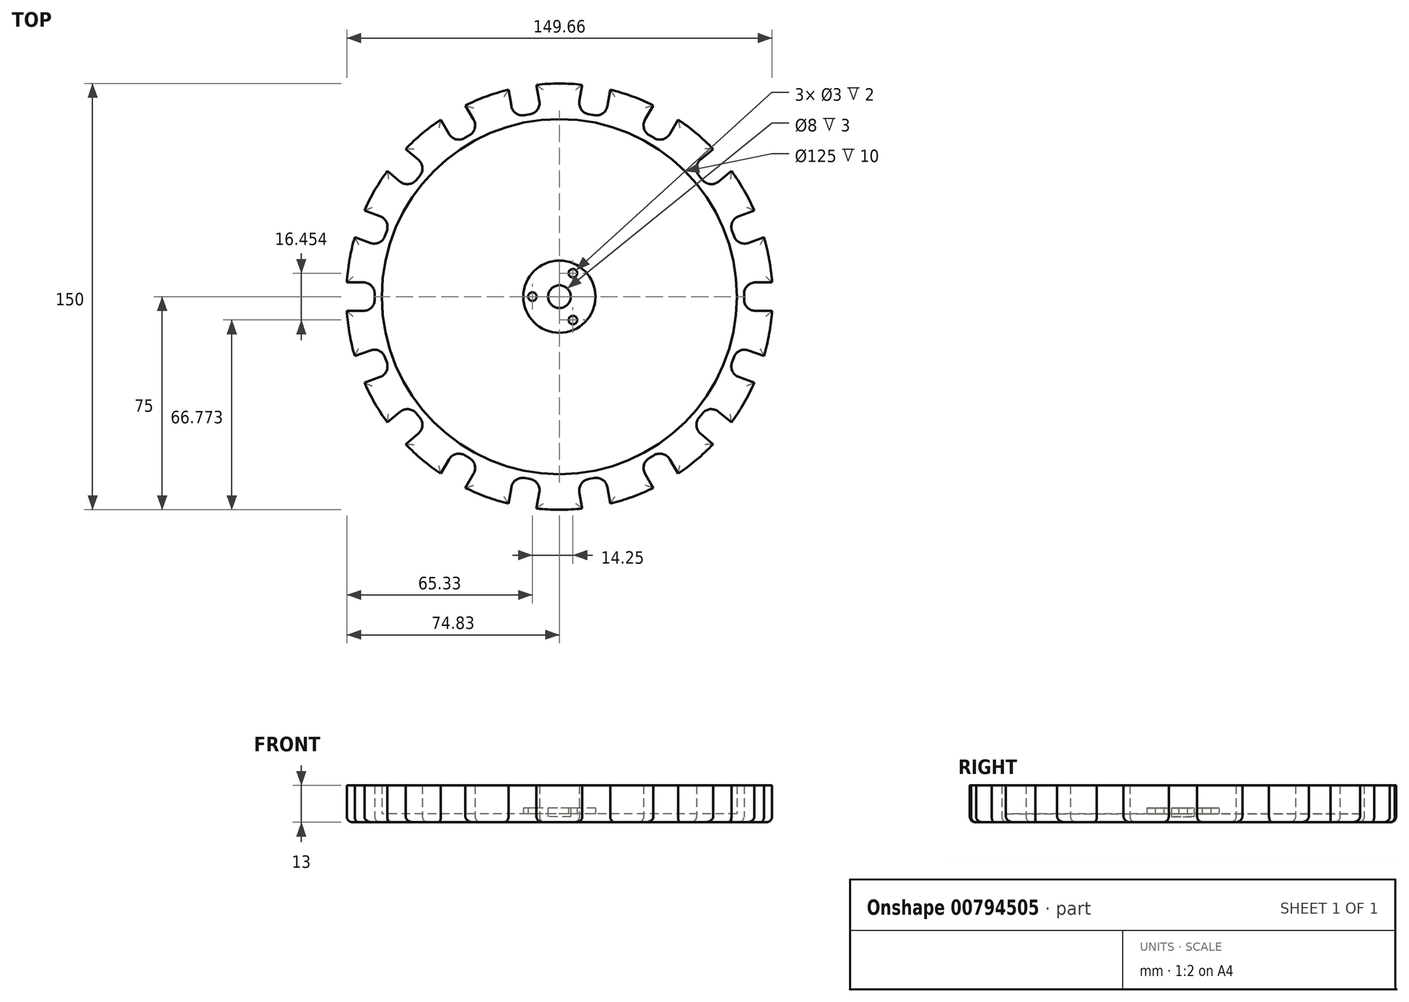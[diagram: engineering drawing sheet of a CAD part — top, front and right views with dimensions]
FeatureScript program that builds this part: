
annotation { "Feature Type Name" : "Feature", "Feature Type Description" : "" }
export const myFeature = defineFeature(function(context is Context, id is Id, definition is map)
    precondition{}
    {
        {
            var Q0;
            Q0=qCreatedBy(makeId("Top.planeOp"),FACE);
            var sketch = newSketch(context, id + "F0", { "sketchPlane" : qUnion([Q0])});
            skCircle(sketch, "E0", {"center": v(0, 0) * mm, "radius": 75 * mm});
            skCircle(sketch, "E1", {"center": v(0, 0) * mm, "radius": 62.5 * mm});
            skLineSegment(sketch, "E2", {"start": v(0, 0) * mm, "end": v(-124.02, 0) * mm, "construction": true});
            skPoint(sketch, "E3", {"position": v(-75, 0) * mm});
            skLineSegment(sketch, "E4.bottom", {"start": v(-75, -5) * mm, "end": v(-69, -5) * mm});
            skLineSegment(sketch, "E4.top", {"start": v(-75, 5) * mm, "end": v(-69, 5) * mm});
            skLineSegment(sketch, "E4.left", {"start": v(-75, -5) * mm, "end": v(-75, 5) * mm});
            skLineSegment(sketch, "E4.right", {"start": v(-65, -1) * mm, "end": v(-65, 1) * mm});
            skPoint(sketch, "E4.middle", {"position": v(-70, 0) * mm});
            skPoint(sketch, "E5.visualSharp", {"position": v(-65, 5) * mm});
            skArc(sketch, "E5.filletArc", {"start": v(-65, 1) * mm, "mid": v(-66.17, 3.83) * mm, "end": v(-69, 5) * mm});
            skPoint(sketch, "E6.visualSharp", {"position": v(-65, -5) * mm});
            skArc(sketch, "E6.filletArc", {"start": v(-69, -5) * mm, "mid": v(-66.17, -3.83) * mm, "end": v(-65, -1) * mm});
            skPoint(sketch, "E7.center", {"position": v(1.56, 0) * mm});
            skCircle(sketch, "E8", {"center": v(0, 0) * mm, "radius": 4 * mm});
            skCircle(sketch, "E9", {"center": v(0, 0) * mm, "radius": 12.7 * mm});
            skCircle(sketch, "E10", {"center": v(0, 0) * mm, "radius": 9.5 * mm, "construction": true});
            skCircle(sketch, "E11", {"center": v(-9.5, 0) * mm, "radius": 1.5 * mm});
            skCircle(sketch, "E12.1.0", {"center": v(-4.75, -8.23) * mm, "radius": 1.5 * mm});
            skCircle(sketch, "E12.2.0", {"center": v(4.75, -8.23) * mm, "radius": 1.5 * mm});
            skCircle(sketch, "E12.3.0", {"center": v(9.5, 0) * mm, "radius": 1.5 * mm});
            skCircle(sketch, "E12.4.0", {"center": v(4.75, 8.23) * mm, "radius": 1.5 * mm});
            skCircle(sketch, "E12.5.0", {"center": v(-4.75, 8.23) * mm, "radius": 1.5 * mm});
            skPoint(sketch, "E13.1.0", {"position": v(-62.8, -17.53) * mm});
            skPoint(sketch, "E13.1.1", {"position": v(-70.48, -25.65) * mm});
            skPoint(sketch, "E13.1.2", {"position": v(-59.37, -26.93) * mm});
            skPoint(sketch, "E13.1.3", {"position": v(-65.78, -23.94) * mm});
            skArc(sketch, "E13.1.4", {"start": v(-63.13, -28.3) * mm, "mid": v(-60.87, -26.23) * mm, "end": v(-60.74, -23.17) * mm});
            skArc(sketch, "E13.1.5", {"start": v(-61.42, -21.3) * mm, "mid": v(-63.5, -19.03) * mm, "end": v(-66.55, -18.9) * mm});
            skLineSegment(sketch, "E13.1.6", {"start": v(-68.77, -30.35) * mm, "end": v(-72.19, -20.95) * mm});
            skLineSegment(sketch, "E13.1.7", {"start": v(-60.74, -23.17) * mm, "end": v(-61.42, -21.3) * mm});
            skLineSegment(sketch, "E13.1.8", {"start": v(-72.19, -20.95) * mm, "end": v(-66.55, -18.9) * mm});
            skLineSegment(sketch, "E13.1.9", {"start": v(-68.77, -30.35) * mm, "end": v(-63.13, -28.3) * mm});
            skPoint(sketch, "E13.2.0", {"position": v(-53, -37.95) * mm});
            skPoint(sketch, "E13.2.1", {"position": v(-57.45, -48.2) * mm});
            skPoint(sketch, "E13.2.2", {"position": v(-46.58, -45.61) * mm});
            skPoint(sketch, "E13.2.3", {"position": v(-53.62, -45) * mm});
            skArc(sketch, "E13.2.4", {"start": v(-49.64, -48.18) * mm, "mid": v(-48.23, -45.47) * mm, "end": v(-49.15, -42.55) * mm});
            skArc(sketch, "E13.2.5", {"start": v(-50.44, -41.02) * mm, "mid": v(-53.15, -39.6) * mm, "end": v(-56.07, -40.52) * mm});
            skLineSegment(sketch, "E13.2.6", {"start": v(-54.24, -52.04) * mm, "end": v(-60.67, -44.38) * mm});
            skLineSegment(sketch, "E13.2.7", {"start": v(-49.15, -42.55) * mm, "end": v(-50.44, -41.02) * mm});
            skLineSegment(sketch, "E13.2.8", {"start": v(-60.67, -44.38) * mm, "end": v(-56.07, -40.52) * mm});
            skLineSegment(sketch, "E13.2.9", {"start": v(-54.24, -52.04) * mm, "end": v(-49.64, -48.18) * mm});
            skPoint(sketch, "E13.3.0", {"position": v(-36.83, -53.8) * mm});
            skPoint(sketch, "E13.3.1", {"position": v(-37.5, -64.95) * mm});
            skPoint(sketch, "E13.3.2", {"position": v(-28.17, -58.8) * mm});
            skPoint(sketch, "E13.3.3", {"position": v(-35, -60.62) * mm});
            skArc(sketch, "E13.3.4", {"start": v(-30.17, -62.26) * mm, "mid": v(-29.77, -59.22) * mm, "end": v(-31.63, -56.8) * mm});
            skArc(sketch, "E13.3.5", {"start": v(-33.37, -55.8) * mm, "mid": v(-36.4, -55.4) * mm, "end": v(-38.83, -57.26) * mm});
            skLineSegment(sketch, "E13.3.6", {"start": v(-33.17, -67.45) * mm, "end": v(-41.83, -62.45) * mm});
            skLineSegment(sketch, "E13.3.7", {"start": v(-31.63, -56.8) * mm, "end": v(-33.37, -55.8) * mm});
            skLineSegment(sketch, "E13.3.8", {"start": v(-41.83, -62.45) * mm, "end": v(-38.83, -57.26) * mm});
            skLineSegment(sketch, "E13.3.9", {"start": v(-33.17, -67.45) * mm, "end": v(-30.17, -62.26) * mm});
            skPoint(sketch, "E13.4.0", {"position": v(-16.21, -63.14) * mm});
            skPoint(sketch, "E13.4.1", {"position": v(-13.02, -73.86) * mm});
            skPoint(sketch, "E13.4.2", {"position": v(-6.36, -64.88) * mm});
            skPoint(sketch, "E13.4.3", {"position": v(-12.16, -68.94) * mm});
            skArc(sketch, "E13.4.4", {"start": v(-7.06, -68.82) * mm, "mid": v(-7.72, -65.83) * mm, "end": v(-10.3, -64.19) * mm});
            skArc(sketch, "E13.4.5", {"start": v(-12.27, -63.84) * mm, "mid": v(-15.26, -64.5) * mm, "end": v(-16.9, -67.08) * mm});
            skLineSegment(sketch, "E13.4.6", {"start": v(-8.1, -74.73) * mm, "end": v(-17.95, -73) * mm});
            skLineSegment(sketch, "E13.4.7", {"start": v(-10.3, -64.19) * mm, "end": v(-12.27, -63.84) * mm});
            skLineSegment(sketch, "E13.4.8", {"start": v(-17.95, -73) * mm, "end": v(-16.9, -67.08) * mm});
            skLineSegment(sketch, "E13.4.9", {"start": v(-8.1, -74.73) * mm, "end": v(-7.06, -68.82) * mm});
            skPoint(sketch, "E13.5.0", {"position": v(6.36, -64.88) * mm});
            skPoint(sketch, "E13.5.1", {"position": v(13.02, -73.86) * mm});
            skPoint(sketch, "E13.5.2", {"position": v(16.21, -63.14) * mm});
            skPoint(sketch, "E13.5.3", {"position": v(12.16, -68.94) * mm});
            skArc(sketch, "E13.5.4", {"start": v(16.9, -67.08) * mm, "mid": v(15.26, -64.5) * mm, "end": v(12.27, -63.84) * mm});
            skArc(sketch, "E13.5.5", {"start": v(10.3, -64.19) * mm, "mid": v(7.72, -65.83) * mm, "end": v(7.06, -68.82) * mm});
            skLineSegment(sketch, "E13.5.6", {"start": v(17.95, -73) * mm, "end": v(8.1, -74.73) * mm});
            skLineSegment(sketch, "E13.5.7", {"start": v(12.27, -63.84) * mm, "end": v(10.3, -64.19) * mm});
            skLineSegment(sketch, "E13.5.8", {"start": v(8.1, -74.73) * mm, "end": v(7.06, -68.82) * mm});
            skLineSegment(sketch, "E13.5.9", {"start": v(17.95, -73) * mm, "end": v(16.9, -67.08) * mm});
            skPoint(sketch, "E13.6.0", {"position": v(28.17, -58.8) * mm});
            skPoint(sketch, "E13.6.1", {"position": v(37.5, -64.95) * mm});
            skPoint(sketch, "E13.6.2", {"position": v(36.83, -53.8) * mm});
            skPoint(sketch, "E13.6.3", {"position": v(35, -60.62) * mm});
            skArc(sketch, "E13.6.4", {"start": v(38.83, -57.26) * mm, "mid": v(36.4, -55.4) * mm, "end": v(33.37, -55.8) * mm});
            skArc(sketch, "E13.6.5", {"start": v(31.63, -56.8) * mm, "mid": v(29.77, -59.22) * mm, "end": v(30.17, -62.26) * mm});
            skLineSegment(sketch, "E13.6.6", {"start": v(41.83, -62.45) * mm, "end": v(33.17, -67.45) * mm});
            skLineSegment(sketch, "E13.6.7", {"start": v(33.37, -55.8) * mm, "end": v(31.63, -56.8) * mm});
            skLineSegment(sketch, "E13.6.8", {"start": v(33.17, -67.45) * mm, "end": v(30.17, -62.26) * mm});
            skLineSegment(sketch, "E13.6.9", {"start": v(41.83, -62.45) * mm, "end": v(38.83, -57.26) * mm});
            skPoint(sketch, "E13.7.0", {"position": v(46.58, -45.61) * mm});
            skPoint(sketch, "E13.7.1", {"position": v(57.45, -48.2) * mm});
            skPoint(sketch, "E13.7.2", {"position": v(53, -37.95) * mm});
            skPoint(sketch, "E13.7.3", {"position": v(53.62, -45) * mm});
            skArc(sketch, "E13.7.4", {"start": v(56.07, -40.52) * mm, "mid": v(53.15, -39.6) * mm, "end": v(50.44, -41.02) * mm});
            skArc(sketch, "E13.7.5", {"start": v(49.15, -42.55) * mm, "mid": v(48.23, -45.47) * mm, "end": v(49.64, -48.18) * mm});
            skLineSegment(sketch, "E13.7.6", {"start": v(60.67, -44.38) * mm, "end": v(54.24, -52.04) * mm});
            skLineSegment(sketch, "E13.7.7", {"start": v(50.44, -41.02) * mm, "end": v(49.15, -42.55) * mm});
            skLineSegment(sketch, "E13.7.8", {"start": v(54.24, -52.04) * mm, "end": v(49.64, -48.18) * mm});
            skLineSegment(sketch, "E13.7.9", {"start": v(60.67, -44.38) * mm, "end": v(56.07, -40.52) * mm});
            skPoint(sketch, "E13.8.0", {"position": v(59.37, -26.93) * mm});
            skPoint(sketch, "E13.8.1", {"position": v(70.48, -25.65) * mm});
            skPoint(sketch, "E13.8.2", {"position": v(62.8, -17.53) * mm});
            skPoint(sketch, "E13.8.3", {"position": v(65.78, -23.94) * mm});
            skArc(sketch, "E13.8.4", {"start": v(66.55, -18.9) * mm, "mid": v(63.5, -19.03) * mm, "end": v(61.42, -21.3) * mm});
            skArc(sketch, "E13.8.5", {"start": v(60.74, -23.17) * mm, "mid": v(60.87, -26.23) * mm, "end": v(63.13, -28.3) * mm});
            skLineSegment(sketch, "E13.8.6", {"start": v(72.19, -20.95) * mm, "end": v(68.77, -30.35) * mm});
            skLineSegment(sketch, "E13.8.7", {"start": v(61.42, -21.3) * mm, "end": v(60.74, -23.17) * mm});
            skLineSegment(sketch, "E13.8.8", {"start": v(68.77, -30.35) * mm, "end": v(63.13, -28.3) * mm});
            skLineSegment(sketch, "E13.8.9", {"start": v(72.19, -20.95) * mm, "end": v(66.55, -18.9) * mm});
            skPoint(sketch, "E13.9.0", {"position": v(65, -5) * mm});
            skPoint(sketch, "E13.9.1", {"position": v(75, 0) * mm});
            skPoint(sketch, "E13.9.2", {"position": v(65, 5) * mm});
            skPoint(sketch, "E13.9.3", {"position": v(70, 0) * mm});
            skArc(sketch, "E13.9.4", {"start": v(69, 5) * mm, "mid": v(66.17, 3.83) * mm, "end": v(65, 1) * mm});
            skArc(sketch, "E13.9.5", {"start": v(65, -1) * mm, "mid": v(66.17, -3.83) * mm, "end": v(69, -5) * mm});
            skLineSegment(sketch, "E13.9.6", {"start": v(75, 5) * mm, "end": v(75, -5) * mm});
            skLineSegment(sketch, "E13.9.7", {"start": v(65, 1) * mm, "end": v(65, -1) * mm});
            skLineSegment(sketch, "E13.9.8", {"start": v(75, -5) * mm, "end": v(69, -5) * mm});
            skLineSegment(sketch, "E13.9.9", {"start": v(75, 5) * mm, "end": v(69, 5) * mm});
            skPoint(sketch, "E13.10.0", {"position": v(62.8, 17.53) * mm});
            skPoint(sketch, "E13.10.1", {"position": v(70.48, 25.65) * mm});
            skPoint(sketch, "E13.10.2", {"position": v(59.37, 26.93) * mm});
            skPoint(sketch, "E13.10.3", {"position": v(65.78, 23.94) * mm});
            skArc(sketch, "E13.10.4", {"start": v(63.13, 28.3) * mm, "mid": v(60.87, 26.23) * mm, "end": v(60.74, 23.17) * mm});
            skArc(sketch, "E13.10.5", {"start": v(61.42, 21.3) * mm, "mid": v(63.5, 19.03) * mm, "end": v(66.55, 18.9) * mm});
            skLineSegment(sketch, "E13.10.6", {"start": v(68.77, 30.35) * mm, "end": v(72.19, 20.95) * mm});
            skLineSegment(sketch, "E13.10.7", {"start": v(60.74, 23.17) * mm, "end": v(61.42, 21.3) * mm});
            skLineSegment(sketch, "E13.10.8", {"start": v(72.19, 20.95) * mm, "end": v(66.55, 18.9) * mm});
            skLineSegment(sketch, "E13.10.9", {"start": v(68.77, 30.35) * mm, "end": v(63.13, 28.3) * mm});
            skPoint(sketch, "E13.11.0", {"position": v(53, 37.95) * mm});
            skPoint(sketch, "E13.11.1", {"position": v(57.45, 48.2) * mm});
            skPoint(sketch, "E13.11.2", {"position": v(46.58, 45.61) * mm});
            skPoint(sketch, "E13.11.3", {"position": v(53.62, 45) * mm});
            skArc(sketch, "E13.11.4", {"start": v(49.64, 48.18) * mm, "mid": v(48.23, 45.47) * mm, "end": v(49.15, 42.55) * mm});
            skArc(sketch, "E13.11.5", {"start": v(50.44, 41.02) * mm, "mid": v(53.15, 39.6) * mm, "end": v(56.07, 40.52) * mm});
            skLineSegment(sketch, "E13.11.6", {"start": v(54.24, 52.04) * mm, "end": v(60.67, 44.38) * mm});
            skLineSegment(sketch, "E13.11.7", {"start": v(49.15, 42.55) * mm, "end": v(50.44, 41.02) * mm});
            skLineSegment(sketch, "E13.11.8", {"start": v(60.67, 44.38) * mm, "end": v(56.07, 40.52) * mm});
            skLineSegment(sketch, "E13.11.9", {"start": v(54.24, 52.04) * mm, "end": v(49.64, 48.18) * mm});
            skPoint(sketch, "E13.12.0", {"position": v(36.83, 53.8) * mm});
            skPoint(sketch, "E13.12.1", {"position": v(37.5, 64.95) * mm});
            skPoint(sketch, "E13.12.2", {"position": v(28.17, 58.8) * mm});
            skPoint(sketch, "E13.12.3", {"position": v(35, 60.62) * mm});
            skArc(sketch, "E13.12.4", {"start": v(30.17, 62.26) * mm, "mid": v(29.77, 59.22) * mm, "end": v(31.63, 56.8) * mm});
            skArc(sketch, "E13.12.5", {"start": v(33.37, 55.8) * mm, "mid": v(36.4, 55.4) * mm, "end": v(38.83, 57.26) * mm});
            skLineSegment(sketch, "E13.12.6", {"start": v(33.17, 67.45) * mm, "end": v(41.83, 62.45) * mm});
            skLineSegment(sketch, "E13.12.7", {"start": v(31.63, 56.8) * mm, "end": v(33.37, 55.8) * mm});
            skLineSegment(sketch, "E13.12.8", {"start": v(41.83, 62.45) * mm, "end": v(38.83, 57.26) * mm});
            skLineSegment(sketch, "E13.12.9", {"start": v(33.17, 67.45) * mm, "end": v(30.17, 62.26) * mm});
            skPoint(sketch, "E13.13.0", {"position": v(16.21, 63.14) * mm});
            skPoint(sketch, "E13.13.1", {"position": v(13.02, 73.86) * mm});
            skPoint(sketch, "E13.13.2", {"position": v(6.36, 64.88) * mm});
            skPoint(sketch, "E13.13.3", {"position": v(12.16, 68.94) * mm});
            skArc(sketch, "E13.13.4", {"start": v(7.06, 68.82) * mm, "mid": v(7.72, 65.83) * mm, "end": v(10.3, 64.19) * mm});
            skArc(sketch, "E13.13.5", {"start": v(12.27, 63.84) * mm, "mid": v(15.26, 64.5) * mm, "end": v(16.9, 67.08) * mm});
            skLineSegment(sketch, "E13.13.6", {"start": v(8.1, 74.73) * mm, "end": v(17.95, 73) * mm});
            skLineSegment(sketch, "E13.13.7", {"start": v(10.3, 64.19) * mm, "end": v(12.27, 63.84) * mm});
            skLineSegment(sketch, "E13.13.8", {"start": v(17.95, 73) * mm, "end": v(16.9, 67.08) * mm});
            skLineSegment(sketch, "E13.13.9", {"start": v(8.1, 74.73) * mm, "end": v(7.06, 68.82) * mm});
            skPoint(sketch, "E13.14.0", {"position": v(-6.36, 64.88) * mm});
            skPoint(sketch, "E13.14.1", {"position": v(-13.02, 73.86) * mm});
            skPoint(sketch, "E13.14.2", {"position": v(-16.21, 63.14) * mm});
            skPoint(sketch, "E13.14.3", {"position": v(-12.16, 68.94) * mm});
            skArc(sketch, "E13.14.4", {"start": v(-16.9, 67.08) * mm, "mid": v(-15.26, 64.5) * mm, "end": v(-12.27, 63.84) * mm});
            skArc(sketch, "E13.14.5", {"start": v(-10.3, 64.19) * mm, "mid": v(-7.72, 65.83) * mm, "end": v(-7.06, 68.82) * mm});
            skLineSegment(sketch, "E13.14.6", {"start": v(-17.95, 73) * mm, "end": v(-8.1, 74.73) * mm});
            skLineSegment(sketch, "E13.14.7", {"start": v(-12.27, 63.84) * mm, "end": v(-10.3, 64.19) * mm});
            skLineSegment(sketch, "E13.14.8", {"start": v(-8.1, 74.73) * mm, "end": v(-7.06, 68.82) * mm});
            skLineSegment(sketch, "E13.14.9", {"start": v(-17.95, 73) * mm, "end": v(-16.9, 67.08) * mm});
            skPoint(sketch, "E13.15.0", {"position": v(-28.17, 58.8) * mm});
            skPoint(sketch, "E13.15.1", {"position": v(-37.5, 64.95) * mm});
            skPoint(sketch, "E13.15.2", {"position": v(-36.83, 53.8) * mm});
            skPoint(sketch, "E13.15.3", {"position": v(-35, 60.62) * mm});
            skArc(sketch, "E13.15.4", {"start": v(-38.83, 57.26) * mm, "mid": v(-36.4, 55.4) * mm, "end": v(-33.37, 55.8) * mm});
            skArc(sketch, "E13.15.5", {"start": v(-31.63, 56.8) * mm, "mid": v(-29.77, 59.22) * mm, "end": v(-30.17, 62.26) * mm});
            skLineSegment(sketch, "E13.15.6", {"start": v(-41.83, 62.45) * mm, "end": v(-33.17, 67.45) * mm});
            skLineSegment(sketch, "E13.15.7", {"start": v(-33.37, 55.8) * mm, "end": v(-31.63, 56.8) * mm});
            skLineSegment(sketch, "E13.15.8", {"start": v(-33.17, 67.45) * mm, "end": v(-30.17, 62.26) * mm});
            skLineSegment(sketch, "E13.15.9", {"start": v(-41.83, 62.45) * mm, "end": v(-38.83, 57.26) * mm});
            skPoint(sketch, "E13.16.0", {"position": v(-46.58, 45.61) * mm});
            skPoint(sketch, "E13.16.1", {"position": v(-57.45, 48.2) * mm});
            skPoint(sketch, "E13.16.2", {"position": v(-53, 37.95) * mm});
            skPoint(sketch, "E13.16.3", {"position": v(-53.62, 45) * mm});
            skArc(sketch, "E13.16.4", {"start": v(-56.07, 40.52) * mm, "mid": v(-53.15, 39.6) * mm, "end": v(-50.44, 41.02) * mm});
            skArc(sketch, "E13.16.5", {"start": v(-49.15, 42.55) * mm, "mid": v(-48.23, 45.47) * mm, "end": v(-49.64, 48.18) * mm});
            skLineSegment(sketch, "E13.16.6", {"start": v(-60.67, 44.38) * mm, "end": v(-54.24, 52.04) * mm});
            skLineSegment(sketch, "E13.16.7", {"start": v(-50.44, 41.02) * mm, "end": v(-49.15, 42.55) * mm});
            skLineSegment(sketch, "E13.16.8", {"start": v(-54.24, 52.04) * mm, "end": v(-49.64, 48.18) * mm});
            skLineSegment(sketch, "E13.16.9", {"start": v(-60.67, 44.38) * mm, "end": v(-56.07, 40.52) * mm});
            skPoint(sketch, "E13.17.0", {"position": v(-59.37, 26.93) * mm});
            skPoint(sketch, "E13.17.1", {"position": v(-70.48, 25.65) * mm});
            skPoint(sketch, "E13.17.2", {"position": v(-62.8, 17.53) * mm});
            skPoint(sketch, "E13.17.3", {"position": v(-65.78, 23.94) * mm});
            skArc(sketch, "E13.17.4", {"start": v(-66.55, 18.9) * mm, "mid": v(-63.5, 19.03) * mm, "end": v(-61.42, 21.3) * mm});
            skArc(sketch, "E13.17.5", {"start": v(-60.74, 23.17) * mm, "mid": v(-60.87, 26.23) * mm, "end": v(-63.13, 28.3) * mm});
            skLineSegment(sketch, "E13.17.6", {"start": v(-72.19, 20.95) * mm, "end": v(-68.77, 30.35) * mm});
            skLineSegment(sketch, "E13.17.7", {"start": v(-61.42, 21.3) * mm, "end": v(-60.74, 23.17) * mm});
            skLineSegment(sketch, "E13.17.8", {"start": v(-68.77, 30.35) * mm, "end": v(-63.13, 28.3) * mm});
            skLineSegment(sketch, "E13.17.9", {"start": v(-72.19, 20.95) * mm, "end": v(-66.55, 18.9) * mm});
            skSolve(sketch);
        }
        {
            var Q0;
            Q0=makeQuery(id+"F0.imprint","IMPRINT",FACE,{"disambiguationData":[TD([[makeQuery(id+"F0.imprint","IMPRINT",EDGE,{"derivedFrom":sQuery(id+"F0.wireOp",EDGE,"E1")}),1.0]])]});
            var Q1;
            Q1=makeQuery(id+"F0.imprint","IMPRINT",FACE,{"disambiguationData":[TD([[makeQuery(id+"F0.imprint","IMPRINT",EDGE,{"derivedFrom":sQuery(id+"F0.wireOp",EDGE,"E8")}),-1.0]])]});
            var Q2;
            Q2=makeQuery(id+"F0.imprint","IMPRINT",FACE,{"disambiguationData":[TD([[makeQuery(id+"F0.imprint","IMPRINT",EDGE,{"derivedFrom":sQuery(id+"F0.wireOp",EDGE,"E12.3.0")}),1.0]])]});
            var Q3;
            Q3=makeQuery(id+"F0.imprint","IMPRINT",FACE,{"disambiguationData":[TD([[makeQuery(id+"F0.imprint","IMPRINT",EDGE,{"derivedFrom":sQuery(id+"F0.wireOp",EDGE,"E12.4.0")}),1.0]])]});
            var Q4;
            Q4=makeQuery(id+"F0.imprint","IMPRINT",FACE,{"disambiguationData":[TD([[makeQuery(id+"F0.imprint","IMPRINT",EDGE,{"derivedFrom":sQuery(id+"F0.wireOp",EDGE,"E12.5.0")}),1.0]])]});
            var Q5;
            Q5=makeQuery(id+"F0.imprint","IMPRINT",FACE,{"disambiguationData":[TD([[makeQuery(id+"F0.imprint","IMPRINT",EDGE,{"derivedFrom":sQuery(id+"F0.wireOp",EDGE,"E11")}),1.0]])]});
            var Q6;
            Q6=makeQuery(id+"F0.imprint","IMPRINT",FACE,{"disambiguationData":[TD([[makeQuery(id+"F0.imprint","IMPRINT",EDGE,{"derivedFrom":sQuery(id+"F0.wireOp",EDGE,"E12.1.0")}),1.0]])]});
            var Q7;
            Q7=makeQuery(id+"F0.imprint","IMPRINT",FACE,{"disambiguationData":[TD([[makeQuery(id+"F0.imprint","IMPRINT",EDGE,{"derivedFrom":sQuery(id+"F0.wireOp",EDGE,"E12.2.0")}),1.0]])]});
            extrude(context, id + "F1", {"entities" : qUnion([Q0, Q1, Q2, Q3, Q4, Q5, Q6, Q7]), "depth" : 3 * mm, "offsetDistance" : 25 * mm});
        }
        {
            var Q0;
            Q0=makeQuery(id+"F0.imprint","IMPRINT",FACE,{"disambiguationData":[TD([[makeQuery(id+"F0.imprint","IMPRINT",EDGE,{"derivedFrom":sQuery(id+"F0.wireOp",EDGE,"E1")}),-1.0]])]});
            extrude(context, id + "F2", {"entities" : qUnion([Q0]), "operationType" : NewBodyOperationType.ADD, "depth" : 13 * mm, "offsetDistance" : 25 * mm});
        }
        {
            var Q0;
            Q0=makeQuery(id+"F0.imprint","IMPRINT",FACE,{"disambiguationData":[TD([[makeQuery(id+"F0.imprint","IMPRINT",EDGE,{"derivedFrom":sQuery(id+"F0.wireOp",EDGE,"E8")}),-1.0]])]});
            var Q1;
            Q1=makeQuery(id+"F0.imprint","IMPRINT",FACE,{"disambiguationData":[TD([[makeQuery(id+"F0.imprint","IMPRINT",EDGE,{"derivedFrom":sQuery(id+"F0.wireOp",EDGE,"E12.5.0")}),1.0]])]});
            var Q2;
            Q2=makeQuery(id+"F0.imprint","IMPRINT",FACE,{"disambiguationData":[TD([[makeQuery(id+"F0.imprint","IMPRINT",EDGE,{"derivedFrom":sQuery(id+"F0.wireOp",EDGE,"E12.3.0")}),1.0]])]});
            var Q3;
            Q3=makeQuery(id+"F0.imprint","IMPRINT",FACE,{"disambiguationData":[TD([[makeQuery(id+"F0.imprint","IMPRINT",EDGE,{"derivedFrom":sQuery(id+"F0.wireOp",EDGE,"E12.1.0")}),1.0]])]});
            extrude(context, id + "F3", {"entities" : qUnion([Q0, Q1, Q2, Q3]), "operationType" : NewBodyOperationType.ADD, "depth" : 5 * mm, "offsetDistance" : 25 * mm});
        }
        {
            var Q0;
            Q0=makeQuery(id+"F0.imprint","IMPRINT",FACE,{"disambiguationData":[TD([[makeQuery(id+"F0.imprint","IMPRINT",EDGE,{"derivedFrom":sQuery(id+"F0.wireOp",EDGE,"E8")}),1.0]])]});
            extrude(context, id + "F4", {"entities" : qUnion([Q0]), "operationType" : NewBodyOperationType.ADD, "depth" : 2 * mm, "offsetDistance" : 25 * mm});
        }
        {
            var Q0;
            {var subQ0=sQuery(id+"F0.wireOp",EDGE,"E8");var subQ1=sQuery(id+"F0.wireOp",EDGE,"E1");Q0=makeQuery(id+"F4.boolean.opBoolean","MERGE",FACE,{"derivedFrom":[makeQuery(id+"F2.boolean.opBoolean","MERGE",FACE,{"derivedFrom":[makeQuery(id+"F1.opExtrude","CAP_FACE",FACE,{"disambiguationData":[OSD([subQ1,subQ0])],"isStart":true}),makeQuery(id+"F2.opExtrude","CAP_FACE",FACE,{"disambiguationData":[OSD([sQuery(id+"F0.wireOp",EDGE,"E0"),subQ1,sQuery(id+"F0.wireOp",EDGE,"E4.bottom"),sQuery(id+"F0.wireOp",EDGE,"E4.top"),sQuery(id+"F0.wireOp",EDGE,"E4.right"),sQuery(id+"F0.wireOp",EDGE,"E5.filletArc"),sQuery(id+"F0.wireOp",EDGE,"E6.filletArc"),sQuery(id+"F0.wireOp",EDGE,"E13.1.4"),sQuery(id+"F0.wireOp",EDGE,"E13.1.5"),sQuery(id+"F0.wireOp",EDGE,"E13.1.7"),sQuery(id+"F0.wireOp",EDGE,"E13.1.8"),sQuery(id+"F0.wireOp",EDGE,"E13.1.9"),sQuery(id+"F0.wireOp",EDGE,"E13.2.4"),sQuery(id+"F0.wireOp",EDGE,"E13.2.5"),sQuery(id+"F0.wireOp",EDGE,"E13.2.7"),sQuery(id+"F0.wireOp",EDGE,"E13.2.8"),sQuery(id+"F0.wireOp",EDGE,"E13.2.9"),sQuery(id+"F0.wireOp",EDGE,"E13.3.4"),sQuery(id+"F0.wireOp",EDGE,"E13.3.5"),sQuery(id+"F0.wireOp",EDGE,"E13.3.7"),sQuery(id+"F0.wireOp",EDGE,"E13.3.8"),sQuery(id+"F0.wireOp",EDGE,"E13.3.9"),sQuery(id+"F0.wireOp",EDGE,"E13.4.4"),sQuery(id+"F0.wireOp",EDGE,"E13.4.5"),sQuery(id+"F0.wireOp",EDGE,"E13.4.7"),sQuery(id+"F0.wireOp",EDGE,"E13.4.8"),sQuery(id+"F0.wireOp",EDGE,"E13.4.9"),sQuery(id+"F0.wireOp",EDGE,"E13.5.4"),sQuery(id+"F0.wireOp",EDGE,"E13.5.5"),sQuery(id+"F0.wireOp",EDGE,"E13.5.7"),sQuery(id+"F0.wireOp",EDGE,"E13.5.8"),sQuery(id+"F0.wireOp",EDGE,"E13.5.9"),sQuery(id+"F0.wireOp",EDGE,"E13.6.4"),sQuery(id+"F0.wireOp",EDGE,"E13.6.5"),sQuery(id+"F0.wireOp",EDGE,"E13.6.7"),sQuery(id+"F0.wireOp",EDGE,"E13.6.8"),sQuery(id+"F0.wireOp",EDGE,"E13.6.9"),sQuery(id+"F0.wireOp",EDGE,"E13.7.4"),sQuery(id+"F0.wireOp",EDGE,"E13.7.5"),sQuery(id+"F0.wireOp",EDGE,"E13.7.7"),sQuery(id+"F0.wireOp",EDGE,"E13.7.8"),sQuery(id+"F0.wireOp",EDGE,"E13.7.9"),sQuery(id+"F0.wireOp",EDGE,"E13.8.4"),sQuery(id+"F0.wireOp",EDGE,"E13.8.5"),sQuery(id+"F0.wireOp",EDGE,"E13.8.7"),sQuery(id+"F0.wireOp",EDGE,"E13.8.8"),sQuery(id+"F0.wireOp",EDGE,"E13.8.9"),sQuery(id+"F0.wireOp",EDGE,"E13.9.4"),sQuery(id+"F0.wireOp",EDGE,"E13.9.5"),sQuery(id+"F0.wireOp",EDGE,"E13.9.7"),sQuery(id+"F0.wireOp",EDGE,"E13.9.8"),sQuery(id+"F0.wireOp",EDGE,"E13.9.9"),sQuery(id+"F0.wireOp",EDGE,"E13.10.4"),sQuery(id+"F0.wireOp",EDGE,"E13.10.5"),sQuery(id+"F0.wireOp",EDGE,"E13.10.7"),sQuery(id+"F0.wireOp",EDGE,"E13.10.8"),sQuery(id+"F0.wireOp",EDGE,"E13.10.9"),sQuery(id+"F0.wireOp",EDGE,"E13.11.4"),sQuery(id+"F0.wireOp",EDGE,"E13.11.5"),sQuery(id+"F0.wireOp",EDGE,"E13.11.7"),sQuery(id+"F0.wireOp",EDGE,"E13.11.8"),sQuery(id+"F0.wireOp",EDGE,"E13.11.9"),sQuery(id+"F0.wireOp",EDGE,"E13.12.4"),sQuery(id+"F0.wireOp",EDGE,"E13.12.5"),sQuery(id+"F0.wireOp",EDGE,"E13.12.7"),sQuery(id+"F0.wireOp",EDGE,"E13.12.8"),sQuery(id+"F0.wireOp",EDGE,"E13.12.9"),sQuery(id+"F0.wireOp",EDGE,"E13.13.4"),sQuery(id+"F0.wireOp",EDGE,"E13.13.5"),sQuery(id+"F0.wireOp",EDGE,"E13.13.7"),sQuery(id+"F0.wireOp",EDGE,"E13.13.8"),sQuery(id+"F0.wireOp",EDGE,"E13.13.9"),sQuery(id+"F0.wireOp",EDGE,"E13.14.4"),sQuery(id+"F0.wireOp",EDGE,"E13.14.5"),sQuery(id+"F0.wireOp",EDGE,"E13.14.7"),sQuery(id+"F0.wireOp",EDGE,"E13.14.8"),sQuery(id+"F0.wireOp",EDGE,"E13.14.9"),sQuery(id+"F0.wireOp",EDGE,"E13.15.4"),sQuery(id+"F0.wireOp",EDGE,"E13.15.5"),sQuery(id+"F0.wireOp",EDGE,"E13.15.7"),sQuery(id+"F0.wireOp",EDGE,"E13.15.8"),sQuery(id+"F0.wireOp",EDGE,"E13.15.9"),sQuery(id+"F0.wireOp",EDGE,"E13.16.4"),sQuery(id+"F0.wireOp",EDGE,"E13.16.5"),sQuery(id+"F0.wireOp",EDGE,"E13.16.7"),sQuery(id+"F0.wireOp",EDGE,"E13.16.8"),sQuery(id+"F0.wireOp",EDGE,"E13.16.9"),sQuery(id+"F0.wireOp",EDGE,"E13.17.4"),sQuery(id+"F0.wireOp",EDGE,"E13.17.5"),sQuery(id+"F0.wireOp",EDGE,"E13.17.7"),sQuery(id+"F0.wireOp",EDGE,"E13.17.8"),sQuery(id+"F0.wireOp",EDGE,"E13.17.9")])],"isStart":true})]}),makeQuery(id+"F4.opExtrude","CAP_FACE",FACE,{"disambiguationData":[OSD([subQ0])],"isStart":true})]});}
            fillet(context, id + "F5", {"entities" : qUnion([Q0]), "radius" : 2 * mm, "tangentPropagation" : true, "allowEdgeOverflow" : false});
        }
    });
